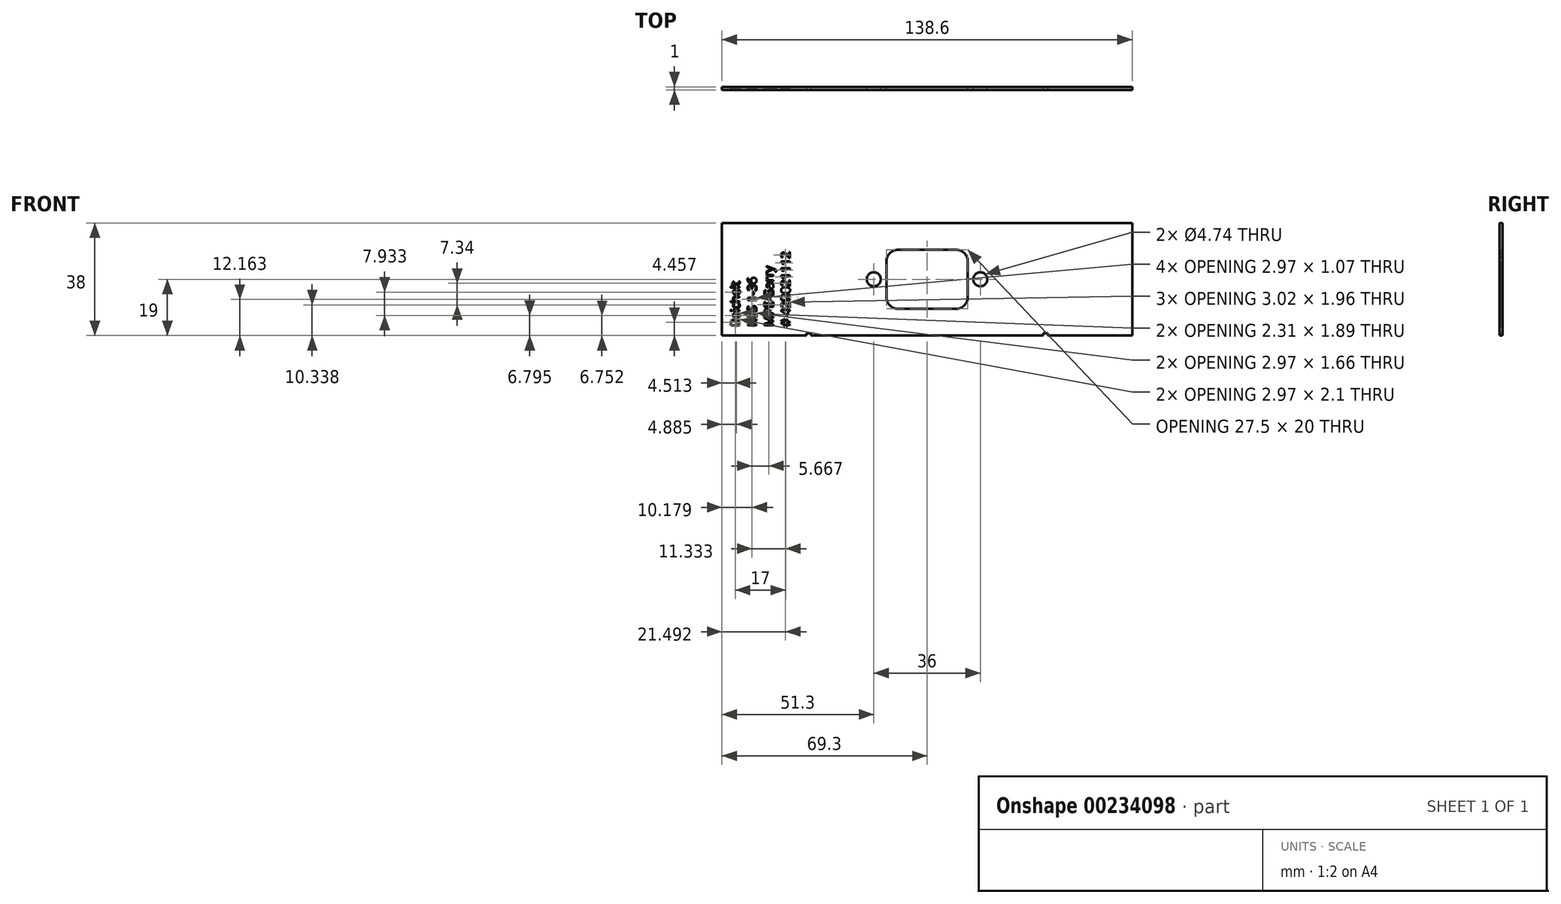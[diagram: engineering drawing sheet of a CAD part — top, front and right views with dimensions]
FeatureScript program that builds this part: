
annotation { "Feature Type Name" : "Feature", "Feature Type Description" : "" }
export const myFeature = defineFeature(function(context is Context, id is Id, definition is map)
    precondition{}
    {
        {
            var Q0;
            Q0=qCreatedBy(makeId("Front.planeOp"),FACE);
            var sketch = newSketch(context, id + "F0", { "sketchPlane" : qUnion([Q0])});
            skLineSegment(sketch, "E0.bottom", {"start": v(9.75, 10) * mm, "end": v(-9.75, 10) * mm});
            skLineSegment(sketch, "E0.top", {"start": v(9.75, -10) * mm, "end": v(-9.75, -10) * mm});
            skLineSegment(sketch, "E0.left", {"start": v(13.75, 6) * mm, "end": v(13.75, -6) * mm});
            skLineSegment(sketch, "E0.right", {"start": v(-13.75, 6) * mm, "end": v(-13.75, -6) * mm});
            skPoint(sketch, "E0.middle", {"position": v(0, 0) * mm});
            skPoint(sketch, "E1.visualSharp", {"position": v(-13.75, 10) * mm});
            skArc(sketch, "E1.filletArc", {"start": v(-9.75, 10) * mm, "mid": v(-12.58, 8.83) * mm, "end": v(-13.75, 6) * mm});
            skPoint(sketch, "E2.visualSharp", {"position": v(-13.75, -10) * mm});
            skArc(sketch, "E2.filletArc", {"start": v(-13.75, -6) * mm, "mid": v(-12.58, -8.83) * mm, "end": v(-9.75, -10) * mm});
            skPoint(sketch, "E3.visualSharp", {"position": v(13.75, -10) * mm});
            skArc(sketch, "E3.filletArc", {"start": v(9.75, -10) * mm, "mid": v(12.58, -8.83) * mm, "end": v(13.75, -6) * mm});
            skPoint(sketch, "E4.visualSharp", {"position": v(13.75, 10) * mm});
            skArc(sketch, "E4.filletArc", {"start": v(13.75, 6) * mm, "mid": v(12.58, 8.83) * mm, "end": v(9.75, 10) * mm});
            skCircle(sketch, "E5", {"center": v(-18, 0) * mm, "radius": 2.37 * mm});
            skCircle(sketch, "E6", {"center": v(18, 0) * mm, "radius": 2.37 * mm});
            skLineSegment(sketch, "E7.bottom", {"start": v(40, 19) * mm, "end": v(-40, 19) * mm});
            skLineSegment(sketch, "E7.top", {"start": v(40, -19) * mm, "end": v(-40, -19) * mm});
            skLineSegment(sketch, "E7.left", {"start": v(40, 19) * mm, "end": v(40, -19) * mm});
            skLineSegment(sketch, "E7.right", {"start": v(-40, 19) * mm, "end": v(-40, -19) * mm});
            skText(sketch, "E8", { "text": "Reichelt\nKES 1-36\nMPE Garry \n# 42R021112", "fontName": "OpenSans-Regular.ttf"});
            skLineSegment(sketch, "E9.bottom", {"start": v(-40, -19) * mm, "end": v(-69.3, -19) * mm});
            skLineSegment(sketch, "E9.top", {"start": v(-40, 19) * mm, "end": v(-69.3, 19) * mm});
            skLineSegment(sketch, "E9.left", {"start": v(-40, -19) * mm, "end": v(-40, 19) * mm});
            skLineSegment(sketch, "E9.right", {"start": v(-69.3, -19) * mm, "end": v(-69.3, 19) * mm});
            skLineSegment(sketch, "E10.bottom", {"start": v(40, -19) * mm, "end": v(69.3, -19) * mm});
            skLineSegment(sketch, "E10.top", {"start": v(40, 19) * mm, "end": v(69.3, 19) * mm});
            skLineSegment(sketch, "E10.left", {"start": v(40, -19) * mm, "end": v(40, 19) * mm});
            skLineSegment(sketch, "E10.right", {"start": v(69.3, -19) * mm, "end": v(69.3, 19) * mm});
            skLineSegment(sketch, "E11.bottom", {"start": v(-40, -19) * mm, "end": v(40, -19) * mm});
            skLineSegment(sketch, "E11.top", {"start": v(-40, -32.3) * mm, "end": v(40, -32.3) * mm});
            skLineSegment(sketch, "E11.left", {"start": v(-40, -19) * mm, "end": v(-40, -32.3) * mm});
            skLineSegment(sketch, "E11.right", {"start": v(40, -19) * mm, "end": v(40, -32.3) * mm});
            const initialGuessF0  = {"E8": [-0.0633, -0.016, 0, 1, 0.003]};
            skSetInitialGuess(sketch, initialGuessF0);
            skSolve(sketch);
        }
        {
            var Q0;
            Q0=makeQuery(id+"F0.imprint","IMPRINT",FACE,{"disambiguationData":[TD([[makeQuery(id+"F0.imprint","IMPRINT",EDGE,{"derivedFrom":sQuery(id+"F0.wireOp",EDGE,"E8.sketch_text.stroke-0")}),1.0]])]});
            var Q1;
            Q1=makeQuery(id+"F0.imprint","IMPRINT",FACE,{"disambiguationData":[TD([[makeQuery(id+"F0.imprint","IMPRINT",EDGE,{"derivedFrom":sQuery(id+"F0.wireOp",EDGE,"E0.bottom")}),-1.0]])]});
            var Q2;
            Q2=makeQuery(id+"F0.imprint","IMPRINT",FACE,{"disambiguationData":[TD([[makeQuery(id+"F0.imprint","IMPRINT",EDGE,{"derivedFrom":sQuery(id+"F0.wireOp",EDGE,"E10.bottom")}),1.0]])]});
            var Q3;
            Q3=makeQuery(id+"F0.imprint","IMPRINT",FACE,{"disambiguationData":[TD([[makeQuery(id+"F0.imprint","IMPRINT",EDGE,{"derivedFrom":sQuery(id+"F0.wireOp",EDGE,"E11.bottom")}),-1.0]])]});
            extrude(context, id + "F1", {"entities" : qUnion([Q0, Q1, Q2, Q3]), "endBound" : BoundingType.SYMMETRIC, "depth" : 1 * mm});
        }
        {
            var Q0;
            Q0=makeQuery(id+"F1.opExtrude","CAP_FACE",FACE,{"disambiguationData":[OSD([sQuery(id+"F0.wireOp",EDGE,"E0.bottom"),sQuery(id+"F0.wireOp",EDGE,"E0.top"),sQuery(id+"F0.wireOp",EDGE,"E0.left"),sQuery(id+"F0.wireOp",EDGE,"E0.right"),sQuery(id+"F0.wireOp",EDGE,"E1.filletArc"),sQuery(id+"F0.wireOp",EDGE,"E2.filletArc"),sQuery(id+"F0.wireOp",EDGE,"E3.filletArc"),sQuery(id+"F0.wireOp",EDGE,"E4.filletArc"),sQuery(id+"F0.wireOp",EDGE,"E5"),sQuery(id+"F0.wireOp",EDGE,"E6"),sQuery(id+"F0.wireOp",EDGE,"E7.bottom"),sQuery(id+"F0.wireOp",EDGE,"E8.sketch_text.stroke-0"),sQuery(id+"F0.wireOp",EDGE,"E8.sketch_text.stroke-1"),sQuery(id+"F0.wireOp",EDGE,"E8.sketch_text.stroke-2"),sQuery(id+"F0.wireOp",EDGE,"E8.sketch_text.stroke-3"),sQuery(id+"F0.wireOp",EDGE,"E8.sketch_text.stroke-4"),sQuery(id+"F0.wireOp",EDGE,"E8.sketch_text.stroke-5"),sQuery(id+"F0.wireOp",EDGE,"E8.sketch_text.stroke-6"),sQuery(id+"F0.wireOp",EDGE,"E8.sketch_text.stroke-7"),sQuery(id+"F0.wireOp",EDGE,"E8.sketch_text.stroke-8"),sQuery(id+"F0.wireOp",EDGE,"E8.sketch_text.stroke-9"),sQuery(id+"F0.wireOp",EDGE,"E8.sketch_text.stroke-10"),sQuery(id+"F0.wireOp",EDGE,"E8.sketch_text.stroke-18"),sQuery(id+"F0.wireOp",EDGE,"E8.sketch_text.stroke-19"),sQuery(id+"F0.wireOp",EDGE,"E8.sketch_text.stroke-20"),sQuery(id+"F0.wireOp",EDGE,"E8.sketch_text.stroke-21"),sQuery(id+"F0.wireOp",EDGE,"E8.sketch_text.stroke-22"),sQuery(id+"F0.wireOp",EDGE,"E8.sketch_text.stroke-23"),sQuery(id+"F0.wireOp",EDGE,"E8.sketch_text.stroke-24"),sQuery(id+"F0.wireOp",EDGE,"E8.sketch_text.stroke-25"),sQuery(id+"F0.wireOp",EDGE,"E8.sketch_text.stroke-26"),sQuery(id+"F0.wireOp",EDGE,"E8.sketch_text.stroke-27"),sQuery(id+"F0.wireOp",EDGE,"E8.sketch_text.stroke-28"),sQuery(id+"F0.wireOp",EDGE,"E8.sketch_text.stroke-29"),sQuery(id+"F0.wireOp",EDGE,"E8.sketch_text.stroke-30"),sQuery(id+"F0.wireOp",EDGE,"E8.sketch_text.stroke-31"),sQuery(id+"F0.wireOp",EDGE,"E8.sketch_text.stroke-37"),sQuery(id+"F0.wireOp",EDGE,"E8.sketch_text.stroke-38"),sQuery(id+"F0.wireOp",EDGE,"E8.sketch_text.stroke-39"),sQuery(id+"F0.wireOp",EDGE,"E8.sketch_text.stroke-40"),sQuery(id+"F0.wireOp",EDGE,"E8.sketch_text.stroke-41"),sQuery(id+"F0.wireOp",EDGE,"E8.sketch_text.stroke-42"),sQuery(id+"F0.wireOp",EDGE,"E8.sketch_text.stroke-43"),sQuery(id+"F0.wireOp",EDGE,"E8.sketch_text.stroke-44"),sQuery(id+"F0.wireOp",EDGE,"E8.sketch_text.stroke-45"),sQuery(id+"F0.wireOp",EDGE,"E8.sketch_text.stroke-46"),sQuery(id+"F0.wireOp",EDGE,"E8.sketch_text.stroke-47"),sQuery(id+"F0.wireOp",EDGE,"E8.sketch_text.stroke-48"),sQuery(id+"F0.wireOp",EDGE,"E8.sketch_text.stroke-49"),sQuery(id+"F0.wireOp",EDGE,"E8.sketch_text.stroke-50"),sQuery(id+"F0.wireOp",EDGE,"E8.sketch_text.stroke-51"),sQuery(id+"F0.wireOp",EDGE,"E8.sketch_text.stroke-52"),sQuery(id+"F0.wireOp",EDGE,"E8.sketch_text.stroke-53"),sQuery(id+"F0.wireOp",EDGE,"E8.sketch_text.stroke-54"),sQuery(id+"F0.wireOp",EDGE,"E8.sketch_text.stroke-55"),sQuery(id+"F0.wireOp",EDGE,"E8.sketch_text.stroke-56"),sQuery(id+"F0.wireOp",EDGE,"E8.sketch_text.stroke-57"),sQuery(id+"F0.wireOp",EDGE,"E8.sketch_text.stroke-58"),sQuery(id+"F0.wireOp",EDGE,"E8.sketch_text.stroke-59"),sQuery(id+"F0.wireOp",EDGE,"E8.sketch_text.stroke-60"),sQuery(id+"F0.wireOp",EDGE,"E8.sketch_text.stroke-61"),sQuery(id+"F0.wireOp",EDGE,"E8.sketch_text.stroke-62"),sQuery(id+"F0.wireOp",EDGE,"E8.sketch_text.stroke-63"),sQuery(id+"F0.wireOp",EDGE,"E8.sketch_text.stroke-64"),sQuery(id+"F0.wireOp",EDGE,"E8.sketch_text.stroke-65"),sQuery(id+"F0.wireOp",EDGE,"E8.sketch_text.stroke-66"),sQuery(id+"F0.wireOp",EDGE,"E8.sketch_text.stroke-67"),sQuery(id+"F0.wireOp",EDGE,"E8.sketch_text.stroke-68"),sQuery(id+"F0.wireOp",EDGE,"E8.sketch_text.stroke-69"),sQuery(id+"F0.wireOp",EDGE,"E8.sketch_text.stroke-70"),sQuery(id+"F0.wireOp",EDGE,"E8.sketch_text.stroke-71"),sQuery(id+"F0.wireOp",EDGE,"E8.sketch_text.stroke-72"),sQuery(id+"F0.wireOp",EDGE,"E8.sketch_text.stroke-73"),sQuery(id+"F0.wireOp",EDGE,"E8.sketch_text.stroke-74"),sQuery(id+"F0.wireOp",EDGE,"E8.sketch_text.stroke-75"),sQuery(id+"F0.wireOp",EDGE,"E8.sketch_text.stroke-76"),sQuery(id+"F0.wireOp",EDGE,"E8.sketch_text.stroke-77"),sQuery(id+"F0.wireOp",EDGE,"E8.sketch_text.stroke-78"),sQuery(id+"F0.wireOp",EDGE,"E8.sketch_text.stroke-79"),sQuery(id+"F0.wireOp",EDGE,"E8.sketch_text.stroke-80"),sQuery(id+"F0.wireOp",EDGE,"E8.sketch_text.stroke-81"),sQuery(id+"F0.wireOp",EDGE,"E8.sketch_text.stroke-82"),sQuery(id+"F0.wireOp",EDGE,"E8.sketch_text.stroke-83"),sQuery(id+"F0.wireOp",EDGE,"E8.sketch_text.stroke-84"),sQuery(id+"F0.wireOp",EDGE,"E8.sketch_text.stroke-85"),sQuery(id+"F0.wireOp",EDGE,"E8.sketch_text.stroke-86"),sQuery(id+"F0.wireOp",EDGE,"E8.sketch_text.stroke-87"),sQuery(id+"F0.wireOp",EDGE,"E8.sketch_text.stroke-88"),sQuery(id+"F0.wireOp",EDGE,"E8.sketch_text.stroke-89"),sQuery(id+"F0.wireOp",EDGE,"E8.sketch_text.stroke-90"),sQuery(id+"F0.wireOp",EDGE,"E8.sketch_text.stroke-91"),sQuery(id+"F0.wireOp",EDGE,"E8.sketch_text.stroke-92"),sQuery(id+"F0.wireOp",EDGE,"E8.sketch_text.stroke-93"),sQuery(id+"F0.wireOp",EDGE,"E8.sketch_text.stroke-94"),sQuery(id+"F0.wireOp",EDGE,"E8.sketch_text.stroke-95"),sQuery(id+"F0.wireOp",EDGE,"E8.sketch_text.stroke-101"),sQuery(id+"F0.wireOp",EDGE,"E8.sketch_text.stroke-102"),sQuery(id+"F0.wireOp",EDGE,"E8.sketch_text.stroke-103"),sQuery(id+"F0.wireOp",EDGE,"E8.sketch_text.stroke-104"),sQuery(id+"F0.wireOp",EDGE,"E8.sketch_text.stroke-105"),sQuery(id+"F0.wireOp",EDGE,"E8.sketch_text.stroke-106"),sQuery(id+"F0.wireOp",EDGE,"E8.sketch_text.stroke-107"),sQuery(id+"F0.wireOp",EDGE,"E8.sketch_text.stroke-108"),sQuery(id+"F0.wireOp",EDGE,"E8.sketch_text.stroke-109"),sQuery(id+"F0.wireOp",EDGE,"E8.sketch_text.stroke-110"),sQuery(id+"F0.wireOp",EDGE,"E8.sketch_text.stroke-111"),sQuery(id+"F0.wireOp",EDGE,"E8.sketch_text.stroke-112"),sQuery(id+"F0.wireOp",EDGE,"E8.sketch_text.stroke-113"),sQuery(id+"F0.wireOp",EDGE,"E8.sketch_text.stroke-114"),sQuery(id+"F0.wireOp",EDGE,"E8.sketch_text.stroke-115"),sQuery(id+"F0.wireOp",EDGE,"E8.sketch_text.stroke-116"),sQuery(id+"F0.wireOp",EDGE,"E8.sketch_text.stroke-117"),sQuery(id+"F0.wireOp",EDGE,"E8.sketch_text.stroke-118"),sQuery(id+"F0.wireOp",EDGE,"E8.sketch_text.stroke-119"),sQuery(id+"F0.wireOp",EDGE,"E8.sketch_text.stroke-120"),sQuery(id+"F0.wireOp",EDGE,"E8.sketch_text.stroke-121"),sQuery(id+"F0.wireOp",EDGE,"E8.sketch_text.stroke-122"),sQuery(id+"F0.wireOp",EDGE,"E8.sketch_text.stroke-123"),sQuery(id+"F0.wireOp",EDGE,"E8.sketch_text.stroke-124"),sQuery(id+"F0.wireOp",EDGE,"E8.sketch_text.stroke-125"),sQuery(id+"F0.wireOp",EDGE,"E8.sketch_text.stroke-126"),sQuery(id+"F0.wireOp",EDGE,"E8.sketch_text.stroke-127"),sQuery(id+"F0.wireOp",EDGE,"E8.sketch_text.stroke-128"),sQuery(id+"F0.wireOp",EDGE,"E8.sketch_text.stroke-129"),sQuery(id+"F0.wireOp",EDGE,"E8.sketch_text.stroke-130"),sQuery(id+"F0.wireOp",EDGE,"E8.sketch_text.stroke-131"),sQuery(id+"F0.wireOp",EDGE,"E8.sketch_text.stroke-132"),sQuery(id+"F0.wireOp",EDGE,"E8.sketch_text.stroke-133"),sQuery(id+"F0.wireOp",EDGE,"E8.sketch_text.stroke-134"),sQuery(id+"F0.wireOp",EDGE,"E8.sketch_text.stroke-135"),sQuery(id+"F0.wireOp",EDGE,"E8.sketch_text.stroke-136"),sQuery(id+"F0.wireOp",EDGE,"E8.sketch_text.stroke-137"),sQuery(id+"F0.wireOp",EDGE,"E8.sketch_text.stroke-138"),sQuery(id+"F0.wireOp",EDGE,"E8.sketch_text.stroke-139"),sQuery(id+"F0.wireOp",EDGE,"E8.sketch_text.stroke-140"),sQuery(id+"F0.wireOp",EDGE,"E8.sketch_text.stroke-141"),sQuery(id+"F0.wireOp",EDGE,"E8.sketch_text.stroke-142"),sQuery(id+"F0.wireOp",EDGE,"E8.sketch_text.stroke-143"),sQuery(id+"F0.wireOp",EDGE,"E8.sketch_text.stroke-144"),sQuery(id+"F0.wireOp",EDGE,"E8.sketch_text.stroke-145"),sQuery(id+"F0.wireOp",EDGE,"E8.sketch_text.stroke-146"),sQuery(id+"F0.wireOp",EDGE,"E8.sketch_text.stroke-147"),sQuery(id+"F0.wireOp",EDGE,"E8.sketch_text.stroke-148"),sQuery(id+"F0.wireOp",EDGE,"E8.sketch_text.stroke-149"),sQuery(id+"F0.wireOp",EDGE,"E8.sketch_text.stroke-150"),sQuery(id+"F0.wireOp",EDGE,"E8.sketch_text.stroke-151"),sQuery(id+"F0.wireOp",EDGE,"E8.sketch_text.stroke-152"),sQuery(id+"F0.wireOp",EDGE,"E8.sketch_text.stroke-153"),sQuery(id+"F0.wireOp",EDGE,"E8.sketch_text.stroke-154"),sQuery(id+"F0.wireOp",EDGE,"E8.sketch_text.stroke-155"),sQuery(id+"F0.wireOp",EDGE,"E8.sketch_text.stroke-156"),sQuery(id+"F0.wireOp",EDGE,"E8.sketch_text.stroke-157"),sQuery(id+"F0.wireOp",EDGE,"E8.sketch_text.stroke-158"),sQuery(id+"F0.wireOp",EDGE,"E8.sketch_text.stroke-159"),sQuery(id+"F0.wireOp",EDGE,"E8.sketch_text.stroke-160"),sQuery(id+"F0.wireOp",EDGE,"E8.sketch_text.stroke-161"),sQuery(id+"F0.wireOp",EDGE,"E8.sketch_text.stroke-162"),sQuery(id+"F0.wireOp",EDGE,"E8.sketch_text.stroke-163"),sQuery(id+"F0.wireOp",EDGE,"E8.sketch_text.stroke-164"),sQuery(id+"F0.wireOp",EDGE,"E8.sketch_text.stroke-165"),sQuery(id+"F0.wireOp",EDGE,"E8.sketch_text.stroke-166"),sQuery(id+"F0.wireOp",EDGE,"E8.sketch_text.stroke-167"),sQuery(id+"F0.wireOp",EDGE,"E8.sketch_text.stroke-168"),sQuery(id+"F0.wireOp",EDGE,"E8.sketch_text.stroke-169"),sQuery(id+"F0.wireOp",EDGE,"E8.sketch_text.stroke-170"),sQuery(id+"F0.wireOp",EDGE,"E8.sketch_text.stroke-171"),sQuery(id+"F0.wireOp",EDGE,"E8.sketch_text.stroke-172"),sQuery(id+"F0.wireOp",EDGE,"E8.sketch_text.stroke-173"),sQuery(id+"F0.wireOp",EDGE,"E8.sketch_text.stroke-174"),sQuery(id+"F0.wireOp",EDGE,"E8.sketch_text.stroke-175"),sQuery(id+"F0.wireOp",EDGE,"E8.sketch_text.stroke-176"),sQuery(id+"F0.wireOp",EDGE,"E8.sketch_text.stroke-177"),sQuery(id+"F0.wireOp",EDGE,"E8.sketch_text.stroke-178"),sQuery(id+"F0.wireOp",EDGE,"E8.sketch_text.stroke-179"),sQuery(id+"F0.wireOp",EDGE,"E8.sketch_text.stroke-180"),sQuery(id+"F0.wireOp",EDGE,"E8.sketch_text.stroke-181"),sQuery(id+"F0.wireOp",EDGE,"E8.sketch_text.stroke-182"),sQuery(id+"F0.wireOp",EDGE,"E8.sketch_text.stroke-183"),sQuery(id+"F0.wireOp",EDGE,"E8.sketch_text.stroke-184"),sQuery(id+"F0.wireOp",EDGE,"E8.sketch_text.stroke-185"),sQuery(id+"F0.wireOp",EDGE,"E8.sketch_text.stroke-186"),sQuery(id+"F0.wireOp",EDGE,"E8.sketch_text.stroke-187"),sQuery(id+"F0.wireOp",EDGE,"E8.sketch_text.stroke-188"),sQuery(id+"F0.wireOp",EDGE,"E8.sketch_text.stroke-189"),sQuery(id+"F0.wireOp",EDGE,"E8.sketch_text.stroke-190"),sQuery(id+"F0.wireOp",EDGE,"E8.sketch_text.stroke-191"),sQuery(id+"F0.wireOp",EDGE,"E8.sketch_text.stroke-192"),sQuery(id+"F0.wireOp",EDGE,"E8.sketch_text.stroke-193"),sQuery(id+"F0.wireOp",EDGE,"E8.sketch_text.stroke-194"),sQuery(id+"F0.wireOp",EDGE,"E8.sketch_text.stroke-195"),sQuery(id+"F0.wireOp",EDGE,"E8.sketch_text.stroke-196"),sQuery(id+"F0.wireOp",EDGE,"E8.sketch_text.stroke-197"),sQuery(id+"F0.wireOp",EDGE,"E8.sketch_text.stroke-198"),sQuery(id+"F0.wireOp",EDGE,"E8.sketch_text.stroke-199"),sQuery(id+"F0.wireOp",EDGE,"E8.sketch_text.stroke-200"),sQuery(id+"F0.wireOp",EDGE,"E8.sketch_text.stroke-201"),sQuery(id+"F0.wireOp",EDGE,"E8.sketch_text.stroke-202"),sQuery(id+"F0.wireOp",EDGE,"E8.sketch_text.stroke-203"),sQuery(id+"F0.wireOp",EDGE,"E8.sketch_text.stroke-204"),sQuery(id+"F0.wireOp",EDGE,"E8.sketch_text.stroke-205"),sQuery(id+"F0.wireOp",EDGE,"E8.sketch_text.stroke-206"),sQuery(id+"F0.wireOp",EDGE,"E8.sketch_text.stroke-207"),sQuery(id+"F0.wireOp",EDGE,"E8.sketch_text.stroke-208"),sQuery(id+"F0.wireOp",EDGE,"E8.sketch_text.stroke-209"),sQuery(id+"F0.wireOp",EDGE,"E8.sketch_text.stroke-210"),sQuery(id+"F0.wireOp",EDGE,"E8.sketch_text.stroke-211"),sQuery(id+"F0.wireOp",EDGE,"E8.sketch_text.stroke-212"),sQuery(id+"F0.wireOp",EDGE,"E8.sketch_text.stroke-213"),sQuery(id+"F0.wireOp",EDGE,"E8.sketch_text.stroke-214"),sQuery(id+"F0.wireOp",EDGE,"E8.sketch_text.stroke-215"),sQuery(id+"F0.wireOp",EDGE,"E8.sketch_text.stroke-216"),sQuery(id+"F0.wireOp",EDGE,"E8.sketch_text.stroke-217"),sQuery(id+"F0.wireOp",EDGE,"E8.sketch_text.stroke-218"),sQuery(id+"F0.wireOp",EDGE,"E8.sketch_text.stroke-219"),sQuery(id+"F0.wireOp",EDGE,"E8.sketch_text.stroke-220"),sQuery(id+"F0.wireOp",EDGE,"E8.sketch_text.stroke-221"),sQuery(id+"F0.wireOp",EDGE,"E8.sketch_text.stroke-222"),sQuery(id+"F0.wireOp",EDGE,"E8.sketch_text.stroke-223"),sQuery(id+"F0.wireOp",EDGE,"E8.sketch_text.stroke-224"),sQuery(id+"F0.wireOp",EDGE,"E8.sketch_text.stroke-225"),sQuery(id+"F0.wireOp",EDGE,"E8.sketch_text.stroke-226"),sQuery(id+"F0.wireOp",EDGE,"E8.sketch_text.stroke-227"),sQuery(id+"F0.wireOp",EDGE,"E8.sketch_text.stroke-228"),sQuery(id+"F0.wireOp",EDGE,"E8.sketch_text.stroke-239"),sQuery(id+"F0.wireOp",EDGE,"E8.sketch_text.stroke-240"),sQuery(id+"F0.wireOp",EDGE,"E8.sketch_text.stroke-241"),sQuery(id+"F0.wireOp",EDGE,"E8.sketch_text.stroke-242"),sQuery(id+"F0.wireOp",EDGE,"E8.sketch_text.stroke-243"),sQuery(id+"F0.wireOp",EDGE,"E8.sketch_text.stroke-244"),sQuery(id+"F0.wireOp",EDGE,"E8.sketch_text.stroke-245"),sQuery(id+"F0.wireOp",EDGE,"E8.sketch_text.stroke-246"),sQuery(id+"F0.wireOp",EDGE,"E8.sketch_text.stroke-247"),sQuery(id+"F0.wireOp",EDGE,"E8.sketch_text.stroke-248"),sQuery(id+"F0.wireOp",EDGE,"E8.sketch_text.stroke-249"),sQuery(id+"F0.wireOp",EDGE,"E8.sketch_text.stroke-250"),sQuery(id+"F0.wireOp",EDGE,"E8.sketch_text.stroke-251"),sQuery(id+"F0.wireOp",EDGE,"E8.sketch_text.stroke-252"),sQuery(id+"F0.wireOp",EDGE,"E8.sketch_text.stroke-253"),sQuery(id+"F0.wireOp",EDGE,"E8.sketch_text.stroke-254"),sQuery(id+"F0.wireOp",EDGE,"E8.sketch_text.stroke-255"),sQuery(id+"F0.wireOp",EDGE,"E8.sketch_text.stroke-256"),sQuery(id+"F0.wireOp",EDGE,"E8.sketch_text.stroke-257"),sQuery(id+"F0.wireOp",EDGE,"E8.sketch_text.stroke-258"),sQuery(id+"F0.wireOp",EDGE,"E8.sketch_text.stroke-259"),sQuery(id+"F0.wireOp",EDGE,"E8.sketch_text.stroke-260"),sQuery(id+"F0.wireOp",EDGE,"E8.sketch_text.stroke-261"),sQuery(id+"F0.wireOp",EDGE,"E8.sketch_text.stroke-262"),sQuery(id+"F0.wireOp",EDGE,"E8.sketch_text.stroke-263"),sQuery(id+"F0.wireOp",EDGE,"E8.sketch_text.stroke-264"),sQuery(id+"F0.wireOp",EDGE,"E8.sketch_text.stroke-272"),sQuery(id+"F0.wireOp",EDGE,"E8.sketch_text.stroke-273"),sQuery(id+"F0.wireOp",EDGE,"E8.sketch_text.stroke-274"),sQuery(id+"F0.wireOp",EDGE,"E8.sketch_text.stroke-275"),sQuery(id+"F0.wireOp",EDGE,"E8.sketch_text.stroke-276"),sQuery(id+"F0.wireOp",EDGE,"E8.sketch_text.stroke-277"),sQuery(id+"F0.wireOp",EDGE,"E8.sketch_text.stroke-278"),sQuery(id+"F0.wireOp",EDGE,"E8.sketch_text.stroke-279"),sQuery(id+"F0.wireOp",EDGE,"E8.sketch_text.stroke-280"),sQuery(id+"F0.wireOp",EDGE,"E8.sketch_text.stroke-281"),sQuery(id+"F0.wireOp",EDGE,"E8.sketch_text.stroke-282"),sQuery(id+"F0.wireOp",EDGE,"E8.sketch_text.stroke-283"),sQuery(id+"F0.wireOp",EDGE,"E8.sketch_text.stroke-284"),sQuery(id+"F0.wireOp",EDGE,"E8.sketch_text.stroke-285"),sQuery(id+"F0.wireOp",EDGE,"E8.sketch_text.stroke-286"),sQuery(id+"F0.wireOp",EDGE,"E8.sketch_text.stroke-287"),sQuery(id+"F0.wireOp",EDGE,"E8.sketch_text.stroke-288"),sQuery(id+"F0.wireOp",EDGE,"E8.sketch_text.stroke-289"),sQuery(id+"F0.wireOp",EDGE,"E8.sketch_text.stroke-290"),sQuery(id+"F0.wireOp",EDGE,"E8.sketch_text.stroke-291"),sQuery(id+"F0.wireOp",EDGE,"E8.sketch_text.stroke-292"),sQuery(id+"F0.wireOp",EDGE,"E8.sketch_text.stroke-293"),sQuery(id+"F0.wireOp",EDGE,"E8.sketch_text.stroke-294"),sQuery(id+"F0.wireOp",EDGE,"E8.sketch_text.stroke-295"),sQuery(id+"F0.wireOp",EDGE,"E8.sketch_text.stroke-296"),sQuery(id+"F0.wireOp",EDGE,"E8.sketch_text.stroke-297"),sQuery(id+"F0.wireOp",EDGE,"E8.sketch_text.stroke-298"),sQuery(id+"F0.wireOp",EDGE,"E8.sketch_text.stroke-299"),sQuery(id+"F0.wireOp",EDGE,"E8.sketch_text.stroke-300"),sQuery(id+"F0.wireOp",EDGE,"E8.sketch_text.stroke-301"),sQuery(id+"F0.wireOp",EDGE,"E8.sketch_text.stroke-302"),sQuery(id+"F0.wireOp",EDGE,"E8.sketch_text.stroke-303"),sQuery(id+"F0.wireOp",EDGE,"E8.sketch_text.stroke-304"),sQuery(id+"F0.wireOp",EDGE,"E8.sketch_text.stroke-305"),sQuery(id+"F0.wireOp",EDGE,"E8.sketch_text.stroke-306"),sQuery(id+"F0.wireOp",EDGE,"E8.sketch_text.stroke-307"),sQuery(id+"F0.wireOp",EDGE,"E8.sketch_text.stroke-308"),sQuery(id+"F0.wireOp",EDGE,"E8.sketch_text.stroke-309"),sQuery(id+"F0.wireOp",EDGE,"E8.sketch_text.stroke-310"),sQuery(id+"F0.wireOp",EDGE,"E8.sketch_text.stroke-311"),sQuery(id+"F0.wireOp",EDGE,"E8.sketch_text.stroke-312"),sQuery(id+"F0.wireOp",EDGE,"E8.sketch_text.stroke-313"),sQuery(id+"F0.wireOp",EDGE,"E8.sketch_text.stroke-314"),sQuery(id+"F0.wireOp",EDGE,"E8.sketch_text.stroke-315"),sQuery(id+"F0.wireOp",EDGE,"E8.sketch_text.stroke-316"),sQuery(id+"F0.wireOp",EDGE,"E8.sketch_text.stroke-317"),sQuery(id+"F0.wireOp",EDGE,"E8.sketch_text.stroke-318"),sQuery(id+"F0.wireOp",EDGE,"E8.sketch_text.stroke-319"),sQuery(id+"F0.wireOp",EDGE,"E8.sketch_text.stroke-320"),sQuery(id+"F0.wireOp",EDGE,"E8.sketch_text.stroke-321"),sQuery(id+"F0.wireOp",EDGE,"E8.sketch_text.stroke-322"),sQuery(id+"F0.wireOp",EDGE,"E8.sketch_text.stroke-331"),sQuery(id+"F0.wireOp",EDGE,"E8.sketch_text.stroke-332"),sQuery(id+"F0.wireOp",EDGE,"E8.sketch_text.stroke-333"),sQuery(id+"F0.wireOp",EDGE,"E8.sketch_text.stroke-334"),sQuery(id+"F0.wireOp",EDGE,"E8.sketch_text.stroke-335"),sQuery(id+"F0.wireOp",EDGE,"E8.sketch_text.stroke-336"),sQuery(id+"F0.wireOp",EDGE,"E8.sketch_text.stroke-337"),sQuery(id+"F0.wireOp",EDGE,"E8.sketch_text.stroke-338"),sQuery(id+"F0.wireOp",EDGE,"E8.sketch_text.stroke-339"),sQuery(id+"F0.wireOp",EDGE,"E8.sketch_text.stroke-340"),sQuery(id+"F0.wireOp",EDGE,"E8.sketch_text.stroke-341"),sQuery(id+"F0.wireOp",EDGE,"E8.sketch_text.stroke-342"),sQuery(id+"F0.wireOp",EDGE,"E8.sketch_text.stroke-343"),sQuery(id+"F0.wireOp",EDGE,"E8.sketch_text.stroke-344"),sQuery(id+"F0.wireOp",EDGE,"E8.sketch_text.stroke-345"),sQuery(id+"F0.wireOp",EDGE,"E8.sketch_text.stroke-346"),sQuery(id+"F0.wireOp",EDGE,"E8.sketch_text.stroke-347"),sQuery(id+"F0.wireOp",EDGE,"E8.sketch_text.stroke-348"),sQuery(id+"F0.wireOp",EDGE,"E8.sketch_text.stroke-349"),sQuery(id+"F0.wireOp",EDGE,"E8.sketch_text.stroke-350"),sQuery(id+"F0.wireOp",EDGE,"E8.sketch_text.stroke-351"),sQuery(id+"F0.wireOp",EDGE,"E8.sketch_text.stroke-352"),sQuery(id+"F0.wireOp",EDGE,"E8.sketch_text.stroke-353"),sQuery(id+"F0.wireOp",EDGE,"E8.sketch_text.stroke-354"),sQuery(id+"F0.wireOp",EDGE,"E8.sketch_text.stroke-355"),sQuery(id+"F0.wireOp",EDGE,"E8.sketch_text.stroke-356"),sQuery(id+"F0.wireOp",EDGE,"E8.sketch_text.stroke-357"),sQuery(id+"F0.wireOp",EDGE,"E8.sketch_text.stroke-358"),sQuery(id+"F0.wireOp",EDGE,"E8.sketch_text.stroke-359"),sQuery(id+"F0.wireOp",EDGE,"E8.sketch_text.stroke-360"),sQuery(id+"F0.wireOp",EDGE,"E8.sketch_text.stroke-361"),sQuery(id+"F0.wireOp",EDGE,"E8.sketch_text.stroke-362"),sQuery(id+"F0.wireOp",EDGE,"E8.sketch_text.stroke-363"),sQuery(id+"F0.wireOp",EDGE,"E8.sketch_text.stroke-364"),sQuery(id+"F0.wireOp",EDGE,"E8.sketch_text.stroke-365"),sQuery(id+"F0.wireOp",EDGE,"E8.sketch_text.stroke-366"),sQuery(id+"F0.wireOp",EDGE,"E8.sketch_text.stroke-367"),sQuery(id+"F0.wireOp",EDGE,"E8.sketch_text.stroke-368"),sQuery(id+"F0.wireOp",EDGE,"E8.sketch_text.stroke-369"),sQuery(id+"F0.wireOp",EDGE,"E8.sketch_text.stroke-370"),sQuery(id+"F0.wireOp",EDGE,"E8.sketch_text.stroke-371"),sQuery(id+"F0.wireOp",EDGE,"E8.sketch_text.stroke-372"),sQuery(id+"F0.wireOp",EDGE,"E8.sketch_text.stroke-373"),sQuery(id+"F0.wireOp",EDGE,"E8.sketch_text.stroke-374"),sQuery(id+"F0.wireOp",EDGE,"E8.sketch_text.stroke-375"),sQuery(id+"F0.wireOp",EDGE,"E8.sketch_text.stroke-376"),sQuery(id+"F0.wireOp",EDGE,"E8.sketch_text.stroke-377"),sQuery(id+"F0.wireOp",EDGE,"E8.sketch_text.stroke-378"),sQuery(id+"F0.wireOp",EDGE,"E8.sketch_text.stroke-379"),sQuery(id+"F0.wireOp",EDGE,"E8.sketch_text.stroke-380"),sQuery(id+"F0.wireOp",EDGE,"E8.sketch_text.stroke-381"),sQuery(id+"F0.wireOp",EDGE,"E8.sketch_text.stroke-382"),sQuery(id+"F0.wireOp",EDGE,"E8.sketch_text.stroke-383"),sQuery(id+"F0.wireOp",EDGE,"E8.sketch_text.stroke-384"),sQuery(id+"F0.wireOp",EDGE,"E8.sketch_text.stroke-385"),sQuery(id+"F0.wireOp",EDGE,"E8.sketch_text.stroke-386"),sQuery(id+"F0.wireOp",EDGE,"E8.sketch_text.stroke-387"),sQuery(id+"F0.wireOp",EDGE,"E8.sketch_text.stroke-388"),sQuery(id+"F0.wireOp",EDGE,"E8.sketch_text.stroke-389"),sQuery(id+"F0.wireOp",EDGE,"E8.sketch_text.stroke-390"),sQuery(id+"F0.wireOp",EDGE,"E8.sketch_text.stroke-391"),sQuery(id+"F0.wireOp",EDGE,"E8.sketch_text.stroke-392"),sQuery(id+"F0.wireOp",EDGE,"E8.sketch_text.stroke-393"),sQuery(id+"F0.wireOp",EDGE,"E8.sketch_text.stroke-394"),sQuery(id+"F0.wireOp",EDGE,"E8.sketch_text.stroke-395"),sQuery(id+"F0.wireOp",EDGE,"E8.sketch_text.stroke-396"),sQuery(id+"F0.wireOp",EDGE,"E8.sketch_text.stroke-397"),sQuery(id+"F0.wireOp",EDGE,"E8.sketch_text.stroke-398"),sQuery(id+"F0.wireOp",EDGE,"E8.sketch_text.stroke-399"),sQuery(id+"F0.wireOp",EDGE,"E8.sketch_text.stroke-400"),sQuery(id+"F0.wireOp",EDGE,"E8.sketch_text.stroke-405"),sQuery(id+"F0.wireOp",EDGE,"E8.sketch_text.stroke-406"),sQuery(id+"F0.wireOp",EDGE,"E8.sketch_text.stroke-407"),sQuery(id+"F0.wireOp",EDGE,"E8.sketch_text.stroke-408"),sQuery(id+"F0.wireOp",EDGE,"E8.sketch_text.stroke-409"),sQuery(id+"F0.wireOp",EDGE,"E8.sketch_text.stroke-410"),sQuery(id+"F0.wireOp",EDGE,"E8.sketch_text.stroke-411"),sQuery(id+"F0.wireOp",EDGE,"E8.sketch_text.stroke-412"),sQuery(id+"F0.wireOp",EDGE,"E8.sketch_text.stroke-413"),sQuery(id+"F0.wireOp",EDGE,"E8.sketch_text.stroke-414"),sQuery(id+"F0.wireOp",EDGE,"E8.sketch_text.stroke-415"),sQuery(id+"F0.wireOp",EDGE,"E8.sketch_text.stroke-422"),sQuery(id+"F0.wireOp",EDGE,"E8.sketch_text.stroke-423"),sQuery(id+"F0.wireOp",EDGE,"E8.sketch_text.stroke-424"),sQuery(id+"F0.wireOp",EDGE,"E8.sketch_text.stroke-425"),sQuery(id+"F0.wireOp",EDGE,"E8.sketch_text.stroke-426"),sQuery(id+"F0.wireOp",EDGE,"E8.sketch_text.stroke-427"),sQuery(id+"F0.wireOp",EDGE,"E8.sketch_text.stroke-428"),sQuery(id+"F0.wireOp",EDGE,"E8.sketch_text.stroke-429"),sQuery(id+"F0.wireOp",EDGE,"E8.sketch_text.stroke-430"),sQuery(id+"F0.wireOp",EDGE,"E8.sketch_text.stroke-431"),sQuery(id+"F0.wireOp",EDGE,"E8.sketch_text.stroke-432"),sQuery(id+"F0.wireOp",EDGE,"E8.sketch_text.stroke-433"),sQuery(id+"F0.wireOp",EDGE,"E8.sketch_text.stroke-434"),sQuery(id+"F0.wireOp",EDGE,"E8.sketch_text.stroke-435"),sQuery(id+"F0.wireOp",EDGE,"E8.sketch_text.stroke-436"),sQuery(id+"F0.wireOp",EDGE,"E8.sketch_text.stroke-437"),sQuery(id+"F0.wireOp",EDGE,"E8.sketch_text.stroke-438"),sQuery(id+"F0.wireOp",EDGE,"E8.sketch_text.stroke-439"),sQuery(id+"F0.wireOp",EDGE,"E8.sketch_text.stroke-440"),sQuery(id+"F0.wireOp",EDGE,"E8.sketch_text.stroke-441"),sQuery(id+"F0.wireOp",EDGE,"E8.sketch_text.stroke-442"),sQuery(id+"F0.wireOp",EDGE,"E8.sketch_text.stroke-443"),sQuery(id+"F0.wireOp",EDGE,"E8.sketch_text.stroke-444"),sQuery(id+"F0.wireOp",EDGE,"E8.sketch_text.stroke-445"),sQuery(id+"F0.wireOp",EDGE,"E8.sketch_text.stroke-446"),sQuery(id+"F0.wireOp",EDGE,"E8.sketch_text.stroke-447"),sQuery(id+"F0.wireOp",EDGE,"E8.sketch_text.stroke-448"),sQuery(id+"F0.wireOp",EDGE,"E8.sketch_text.stroke-449"),sQuery(id+"F0.wireOp",EDGE,"E8.sketch_text.stroke-450"),sQuery(id+"F0.wireOp",EDGE,"E8.sketch_text.stroke-451"),sQuery(id+"F0.wireOp",EDGE,"E8.sketch_text.stroke-452"),sQuery(id+"F0.wireOp",EDGE,"E8.sketch_text.stroke-460"),sQuery(id+"F0.wireOp",EDGE,"E8.sketch_text.stroke-461"),sQuery(id+"F0.wireOp",EDGE,"E8.sketch_text.stroke-462"),sQuery(id+"F0.wireOp",EDGE,"E8.sketch_text.stroke-463"),sQuery(id+"F0.wireOp",EDGE,"E8.sketch_text.stroke-464"),sQuery(id+"F0.wireOp",EDGE,"E8.sketch_text.stroke-465"),sQuery(id+"F0.wireOp",EDGE,"E8.sketch_text.stroke-466"),sQuery(id+"F0.wireOp",EDGE,"E8.sketch_text.stroke-467"),sQuery(id+"F0.wireOp",EDGE,"E8.sketch_text.stroke-476"),sQuery(id+"F0.wireOp",EDGE,"E8.sketch_text.stroke-477"),sQuery(id+"F0.wireOp",EDGE,"E8.sketch_text.stroke-478"),sQuery(id+"F0.wireOp",EDGE,"E8.sketch_text.stroke-479"),sQuery(id+"F0.wireOp",EDGE,"E8.sketch_text.stroke-480"),sQuery(id+"F0.wireOp",EDGE,"E8.sketch_text.stroke-481"),sQuery(id+"F0.wireOp",EDGE,"E8.sketch_text.stroke-482"),sQuery(id+"F0.wireOp",EDGE,"E8.sketch_text.stroke-483"),sQuery(id+"F0.wireOp",EDGE,"E8.sketch_text.stroke-484"),sQuery(id+"F0.wireOp",EDGE,"E8.sketch_text.stroke-485"),sQuery(id+"F0.wireOp",EDGE,"E8.sketch_text.stroke-486"),sQuery(id+"F0.wireOp",EDGE,"E8.sketch_text.stroke-487"),sQuery(id+"F0.wireOp",EDGE,"E8.sketch_text.stroke-488"),sQuery(id+"F0.wireOp",EDGE,"E8.sketch_text.stroke-489"),sQuery(id+"F0.wireOp",EDGE,"E8.sketch_text.stroke-490"),sQuery(id+"F0.wireOp",EDGE,"E8.sketch_text.stroke-491"),sQuery(id+"F0.wireOp",EDGE,"E8.sketch_text.stroke-492"),sQuery(id+"F0.wireOp",EDGE,"E8.sketch_text.stroke-493"),sQuery(id+"F0.wireOp",EDGE,"E8.sketch_text.stroke-494"),sQuery(id+"F0.wireOp",EDGE,"E8.sketch_text.stroke-495"),sQuery(id+"F0.wireOp",EDGE,"E8.sketch_text.stroke-496"),sQuery(id+"F0.wireOp",EDGE,"E8.sketch_text.stroke-497"),sQuery(id+"F0.wireOp",EDGE,"E8.sketch_text.stroke-498"),sQuery(id+"F0.wireOp",EDGE,"E8.sketch_text.stroke-499"),sQuery(id+"F0.wireOp",EDGE,"E8.sketch_text.stroke-500"),sQuery(id+"F0.wireOp",EDGE,"E8.sketch_text.stroke-501"),sQuery(id+"F0.wireOp",EDGE,"E8.sketch_text.stroke-502"),sQuery(id+"F0.wireOp",EDGE,"E8.sketch_text.stroke-503"),sQuery(id+"F0.wireOp",EDGE,"E8.sketch_text.stroke-504"),sQuery(id+"F0.wireOp",EDGE,"E8.sketch_text.stroke-505"),sQuery(id+"F0.wireOp",EDGE,"E8.sketch_text.stroke-506"),sQuery(id+"F0.wireOp",EDGE,"E8.sketch_text.stroke-507"),sQuery(id+"F0.wireOp",EDGE,"E8.sketch_text.stroke-508"),sQuery(id+"F0.wireOp",EDGE,"E8.sketch_text.stroke-509"),sQuery(id+"F0.wireOp",EDGE,"E8.sketch_text.stroke-510"),sQuery(id+"F0.wireOp",EDGE,"E8.sketch_text.stroke-511"),sQuery(id+"F0.wireOp",EDGE,"E8.sketch_text.stroke-512"),sQuery(id+"F0.wireOp",EDGE,"E8.sketch_text.stroke-513"),sQuery(id+"F0.wireOp",EDGE,"E8.sketch_text.stroke-514"),sQuery(id+"F0.wireOp",EDGE,"E8.sketch_text.stroke-515"),sQuery(id+"F0.wireOp",EDGE,"E8.sketch_text.stroke-516"),sQuery(id+"F0.wireOp",EDGE,"E8.sketch_text.stroke-517"),sQuery(id+"F0.wireOp",EDGE,"E8.sketch_text.stroke-518"),sQuery(id+"F0.wireOp",EDGE,"E8.sketch_text.stroke-519"),sQuery(id+"F0.wireOp",EDGE,"E8.sketch_text.stroke-520"),sQuery(id+"F0.wireOp",EDGE,"E8.sketch_text.stroke-521"),sQuery(id+"F0.wireOp",EDGE,"E8.sketch_text.stroke-522"),sQuery(id+"F0.wireOp",EDGE,"E8.sketch_text.stroke-523"),sQuery(id+"F0.wireOp",EDGE,"E8.sketch_text.stroke-524"),sQuery(id+"F0.wireOp",EDGE,"E8.sketch_text.stroke-525"),sQuery(id+"F0.wireOp",EDGE,"E8.sketch_text.stroke-526"),sQuery(id+"F0.wireOp",EDGE,"E8.sketch_text.stroke-527"),sQuery(id+"F0.wireOp",EDGE,"E8.sketch_text.stroke-528"),sQuery(id+"F0.wireOp",EDGE,"E8.sketch_text.stroke-529"),sQuery(id+"F0.wireOp",EDGE,"E8.sketch_text.stroke-530"),sQuery(id+"F0.wireOp",EDGE,"E8.sketch_text.stroke-531"),sQuery(id+"F0.wireOp",EDGE,"E8.sketch_text.stroke-532"),sQuery(id+"F0.wireOp",EDGE,"E8.sketch_text.stroke-533"),sQuery(id+"F0.wireOp",EDGE,"E8.sketch_text.stroke-534"),sQuery(id+"F0.wireOp",EDGE,"E8.sketch_text.stroke-535"),sQuery(id+"F0.wireOp",EDGE,"E8.sketch_text.stroke-536"),sQuery(id+"F0.wireOp",EDGE,"E8.sketch_text.stroke-537"),sQuery(id+"F0.wireOp",EDGE,"E8.sketch_text.stroke-538"),sQuery(id+"F0.wireOp",EDGE,"E8.sketch_text.stroke-539"),sQuery(id+"F0.wireOp",EDGE,"E8.sketch_text.stroke-540"),sQuery(id+"F0.wireOp",EDGE,"E8.sketch_text.stroke-541"),sQuery(id+"F0.wireOp",EDGE,"E8.sketch_text.stroke-542"),sQuery(id+"F0.wireOp",EDGE,"E9.bottom"),sQuery(id+"F0.wireOp",EDGE,"E9.top"),sQuery(id+"F0.wireOp",EDGE,"E9.right"),sQuery(id+"F0.wireOp",EDGE,"E10.bottom"),sQuery(id+"F0.wireOp",EDGE,"E10.top"),sQuery(id+"F0.wireOp",EDGE,"E10.right"),sQuery(id+"F0.wireOp",EDGE,"E11.top"),sQuery(id+"F0.wireOp",EDGE,"E11.left"),sQuery(id+"F0.wireOp",EDGE,"E11.right")])],"isStart":false});
            var sketch = newSketch(context, id + "F2", { "sketchPlane" : qUnion([Q0])});
            skLineSegment(sketch, "E12.bottom", {"start": v(-39.25, -18.25) * mm, "end": v(-40.75, -18.25) * mm});
            skLineSegment(sketch, "E12.top", {"start": v(-39.25, -19.75) * mm, "end": v(-40.75, -19.75) * mm});
            skLineSegment(sketch, "E12.left", {"start": v(-39.25, -18.25) * mm, "end": v(-39.25, -19.75) * mm});
            skLineSegment(sketch, "E12.right", {"start": v(-40.75, -18.25) * mm, "end": v(-40.75, -19.75) * mm});
            skPoint(sketch, "E12.middle", {"position": v(-40, -19) * mm});
            skLineSegment(sketch, "E13.bottom", {"start": v(40.75, -18.25) * mm, "end": v(39.25, -18.25) * mm});
            skLineSegment(sketch, "E13.top", {"start": v(40.75, -19.75) * mm, "end": v(39.25, -19.75) * mm});
            skLineSegment(sketch, "E13.left", {"start": v(40.75, -18.25) * mm, "end": v(40.75, -19.75) * mm});
            skLineSegment(sketch, "E13.right", {"start": v(39.25, -18.25) * mm, "end": v(39.25, -19.75) * mm});
            skPoint(sketch, "E13.middle", {"position": v(40, -19) * mm});
            skSolve(sketch);
        }
        {
            var Q0;
            {var subQ1=sQuery(id+"F2.wireOp",EDGE,"E12.bottom");Q0=makeQuery(id+"F2.imprint","IMPRINT",FACE,{"disambiguationData":[TD([[makeQuery(id+"F2.imprint","IMPRINT",EDGE,{"derivedFrom":subQ1}),1.0]])]});}
            var Q1;
            {var subQ2=sQuery(id+"F2.wireOp",EDGE,"E13.bottom");Q1=makeQuery(id+"F2.imprint","IMPRINT",FACE,{"disambiguationData":[TD([[makeQuery(id+"F2.imprint","IMPRINT",EDGE,{"derivedFrom":subQ2}),1.0]])]});}
            extrude(context, id + "F3", {"entities" : qUnion([Q0, Q1]), "operationType" : NewBodyOperationType.REMOVE, "endBound" : BoundingType.UP_TO_NEXT, "oppositeDirection" : true, "depth" : 25 * mm});
        }
    });
